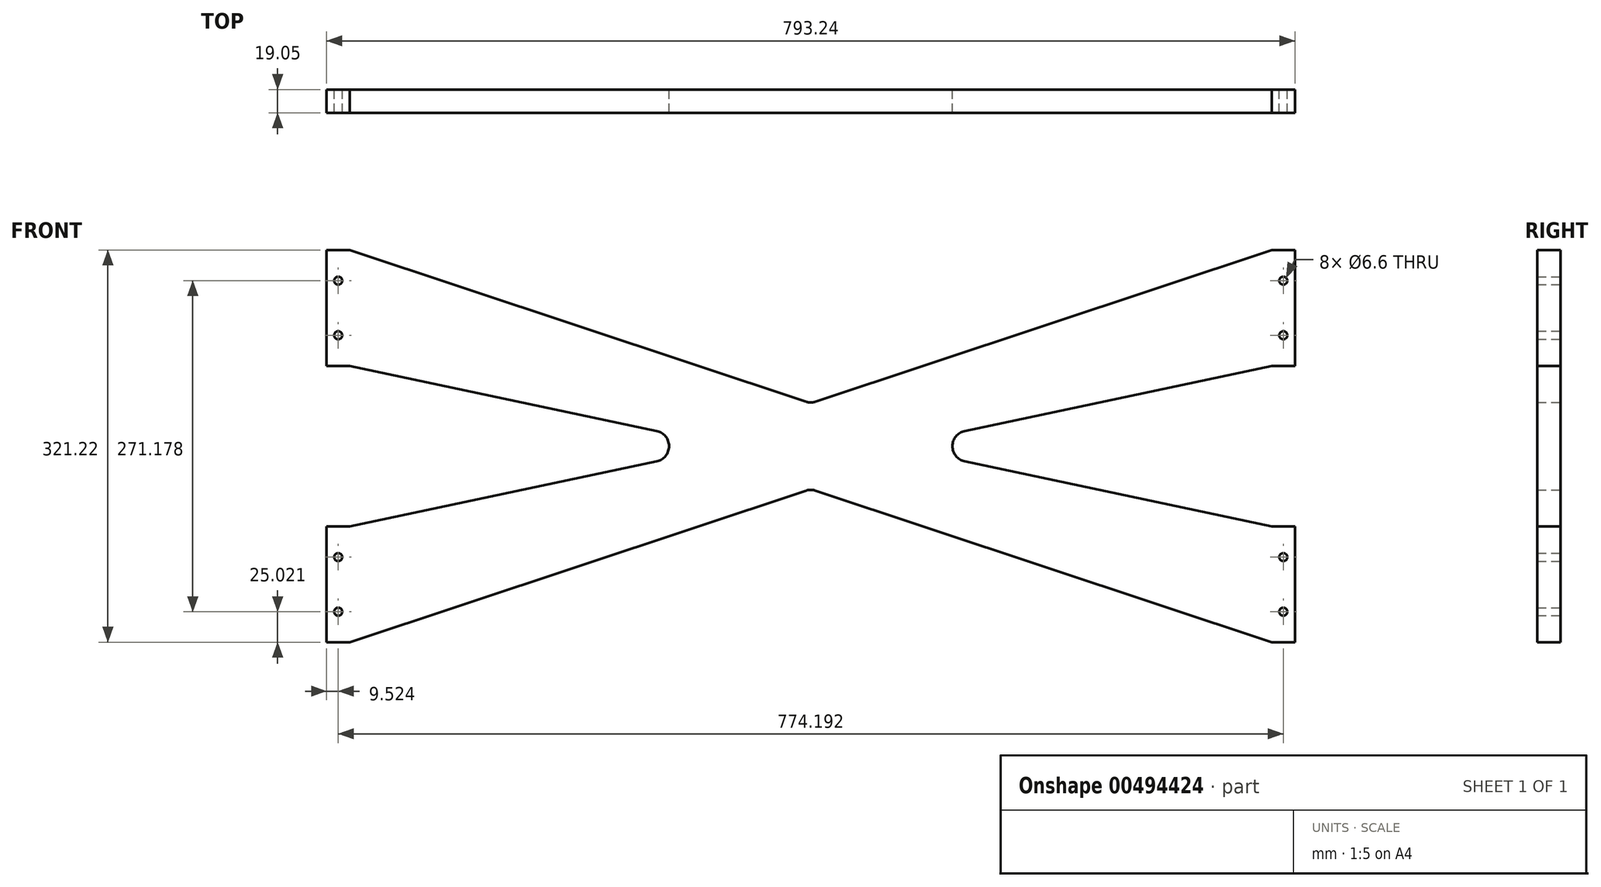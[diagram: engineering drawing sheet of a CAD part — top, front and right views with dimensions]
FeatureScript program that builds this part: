
annotation { "Feature Type Name" : "Feature", "Feature Type Description" : "" }
export const myFeature = defineFeature(function(context is Context, id is Id, definition is map)
    precondition{}
    {
        {
            var Q0;
            Q0=qCreatedBy(makeId("Front.planeOp"),FACE);
            var sketch = newSketch(context, id + "F0", { "sketchPlane" : qUnion([Q0])});
            skLineSegment(sketch, "E0", {"start": v(-377.57, 47.23) * mm, "end": v(435.23, 47.23) * mm, "construction": true});
            skPoint(sketch, "E1.startSnap0", {"position": v(28.83, 47.23) * mm});
            skLineSegment(sketch, "E2", {"start": v(0, 207.84) * mm, "end": v(0, -198.56) * mm, "construction": true});
            skLineSegment(sketch, "E3", {"start": v(-377.57, 113.1) * mm, "end": v(-126.14, 59.65) * mm});
            skLineSegment(sketch, "E4", {"start": v(-377.57, 207.84) * mm, "end": v(-4, 83.67) * mm});
            skLineSegment(sketch, "E5.MirrorCS", {"start": v(-377.57, -113.38) * mm, "end": v(-4, 10.79) * mm});
            skLineSegment(sketch, "E6.MirrorCS", {"start": v(-377.57, -18.64) * mm, "end": v(-126.14, 34.8) * mm});
            skLineSegment(sketch, "E7.MirrorCS", {"start": v(377.57, 207.84) * mm, "end": v(4, 83.67) * mm});
            skLineSegment(sketch, "E8.MirrorCS", {"start": v(377.57, 113.1) * mm, "end": v(126.14, 59.65) * mm});
            skLineSegment(sketch, "E9.MirrorCS", {"start": v(377.57, -18.64) * mm, "end": v(126.14, 34.8) * mm});
            skLineSegment(sketch, "E10.MirrorCS", {"start": v(377.57, -113.38) * mm, "end": v(4, 10.79) * mm});
            skPoint(sketch, "E11.visualSharp", {"position": v(0, 82.34) * mm});
            skArc(sketch, "E11.filletArc", {"start": v(-4, 83.67) * mm, "mid": v(0, 83.02) * mm, "end": v(4, 83.67) * mm});
            skPoint(sketch, "E12.visualSharp", {"position": v(67.7, 47.23) * mm});
            skArc(sketch, "E12.filletArc", {"start": v(126.14, 59.65) * mm, "mid": v(116.08, 47.23) * mm, "end": v(126.14, 34.8) * mm});
            skPoint(sketch, "E13.visualSharp", {"position": v(-67.7, 47.23) * mm});
            skArc(sketch, "E13.filletArc", {"start": v(-126.14, 34.8) * mm, "mid": v(-116.08, 47.23) * mm, "end": v(-126.14, 59.65) * mm});
            skPoint(sketch, "E14.visualSharp", {"position": v(0, 12.12) * mm});
            skArc(sketch, "E14.filletArc", {"start": v(4, 10.79) * mm, "mid": v(0, 11.44) * mm, "end": v(-4, 10.79) * mm});
            skLineSegment(sketch, "E15", {"start": v(-377.57, 207.84) * mm, "end": v(-396.62, 207.84) * mm});
            skLineSegment(sketch, "E16", {"start": v(-396.62, 207.84) * mm, "end": v(-396.62, 113.1) * mm});
            skLineSegment(sketch, "E17", {"start": v(-396.62, 113.1) * mm, "end": v(-377.57, 113.1) * mm});
            skLineSegment(sketch, "E18", {"start": v(-377.57, -18.64) * mm, "end": v(-396.62, -18.64) * mm});
            skLineSegment(sketch, "E19", {"start": v(-396.62, -18.64) * mm, "end": v(-396.62, -113.38) * mm});
            skLineSegment(sketch, "E20", {"start": v(-396.62, -113.38) * mm, "end": v(-377.57, -113.38) * mm});
            skLineSegment(sketch, "E21", {"start": v(377.57, 207.84) * mm, "end": v(396.62, 207.84) * mm});
            skLineSegment(sketch, "E22", {"start": v(396.62, 207.84) * mm, "end": v(396.62, 113.1) * mm});
            skLineSegment(sketch, "E23", {"start": v(396.62, 113.1) * mm, "end": v(377.57, 113.1) * mm});
            skLineSegment(sketch, "E24", {"start": v(377.57, -113.38) * mm, "end": v(396.62, -113.38) * mm});
            skLineSegment(sketch, "E25", {"start": v(396.62, -113.38) * mm, "end": v(396.62, -18.64) * mm});
            skLineSegment(sketch, "E26", {"start": v(396.62, -18.64) * mm, "end": v(377.57, -18.64) * mm});
            skSolve(sketch);
        }
        {
            var Q0;
            Q0=qSketchRegion(id+"F0",true);
            extrude(context, id + "F1", {"entities" : qUnion([Q0]), "depth" : 19.05 * mm});
        }
        {
            var Q0;
            Q0=makeQuery(id+"F0.imprint","IMPRINT",FACE,{"disambiguationData":[TD([[makeQuery(id+"F0.imprint","IMPRINT",EDGE,{"derivedFrom":sQuery(id+"F0.wireOp",EDGE,"E3")}),1.0]])]});
            var sketch = newSketch(context, id + "F2", { "sketchPlane" : qUnion([Q0])});
            skLineSegment(sketch, "E27.0", {"start": v(396.62, 113.1) * mm, "end": v(377.57, 113.1) * mm});
            skLineSegment(sketch, "E28", {"start": v(387.1, 113.1) * mm, "end": v(387.1, 206.1) * mm, "construction": true});
            skCircle(sketch, "E29", {"center": v(387.1, 182.82) * mm, "radius": 3.3 * mm});
            skCircle(sketch, "E30", {"center": v(387.1, 138.11) * mm, "radius": 3.3 * mm});
            skLineSegment(sketch, "E31.0", {"start": v(0, 207.84) * mm, "end": v(0, -198.56) * mm, "construction": true});
            skLineSegment(sketch, "E32.0", {"start": v(-377.57, 47.23) * mm, "end": v(435.23, 47.23) * mm, "construction": true});
            skCircle(sketch, "E33.MirrorC", {"center": v(-387.1, 182.82) * mm, "radius": 3.3 * mm});
            skCircle(sketch, "E34.MirrorC", {"center": v(-387.1, 138.11) * mm, "radius": 3.3 * mm});
            skCircle(sketch, "E35.MirrorC", {"center": v(387.1, -43.65) * mm, "radius": 3.3 * mm});
            skCircle(sketch, "E36.MirrorC", {"center": v(387.1, -88.36) * mm, "radius": 3.3 * mm});
            skCircle(sketch, "E37.MirrorC", {"center": v(-387.1, -88.36) * mm, "radius": 3.3 * mm});
            skCircle(sketch, "E38.MirrorC", {"center": v(-387.1, -43.65) * mm, "radius": 3.3 * mm});
            skSolve(sketch);
        }
        {
            var Q0;
            Q0=qSketchRegion(id+"F2",true);
            var Q1;
            Q1=makeQuery(id+"F1.opExtrude","CAP_FACE",FACE,{"disambiguationData":[OSD([sQuery(id+"F0.wireOp",EDGE,"E3"),sQuery(id+"F0.wireOp",EDGE,"E4"),sQuery(id+"F0.wireOp",EDGE,"E5.MirrorCS"),sQuery(id+"F0.wireOp",EDGE,"E6.MirrorCS"),sQuery(id+"F0.wireOp",EDGE,"E7.MirrorCS"),sQuery(id+"F0.wireOp",EDGE,"E8.MirrorCS"),sQuery(id+"F0.wireOp",EDGE,"E9.MirrorCS"),sQuery(id+"F0.wireOp",EDGE,"E10.MirrorCS"),sQuery(id+"F0.wireOp",EDGE,"E11.filletArc"),sQuery(id+"F0.wireOp",EDGE,"E12.filletArc"),sQuery(id+"F0.wireOp",EDGE,"E13.filletArc"),sQuery(id+"F0.wireOp",EDGE,"E14.filletArc"),sQuery(id+"F0.wireOp",EDGE,"E15"),sQuery(id+"F0.wireOp",EDGE,"E16"),sQuery(id+"F0.wireOp",EDGE,"E17"),sQuery(id+"F0.wireOp",EDGE,"E18"),sQuery(id+"F0.wireOp",EDGE,"E19"),sQuery(id+"F0.wireOp",EDGE,"E20"),sQuery(id+"F0.wireOp",EDGE,"E21"),sQuery(id+"F0.wireOp",EDGE,"E22"),sQuery(id+"F0.wireOp",EDGE,"E23"),sQuery(id+"F0.wireOp",EDGE,"E24"),sQuery(id+"F0.wireOp",EDGE,"E25"),sQuery(id+"F0.wireOp",EDGE,"E26")])],"isStart":false});
            extrude(context, id + "F3", {"entities" : qUnion([Q0]), "operationType" : NewBodyOperationType.REMOVE, "endBound" : BoundingType.UP_TO_SURFACE, "endBoundEntityFace" : qUnion([Q1]), "depth" : 25.4 * mm, "offsetDistance" : 25.4 * mm});
        }
    });
